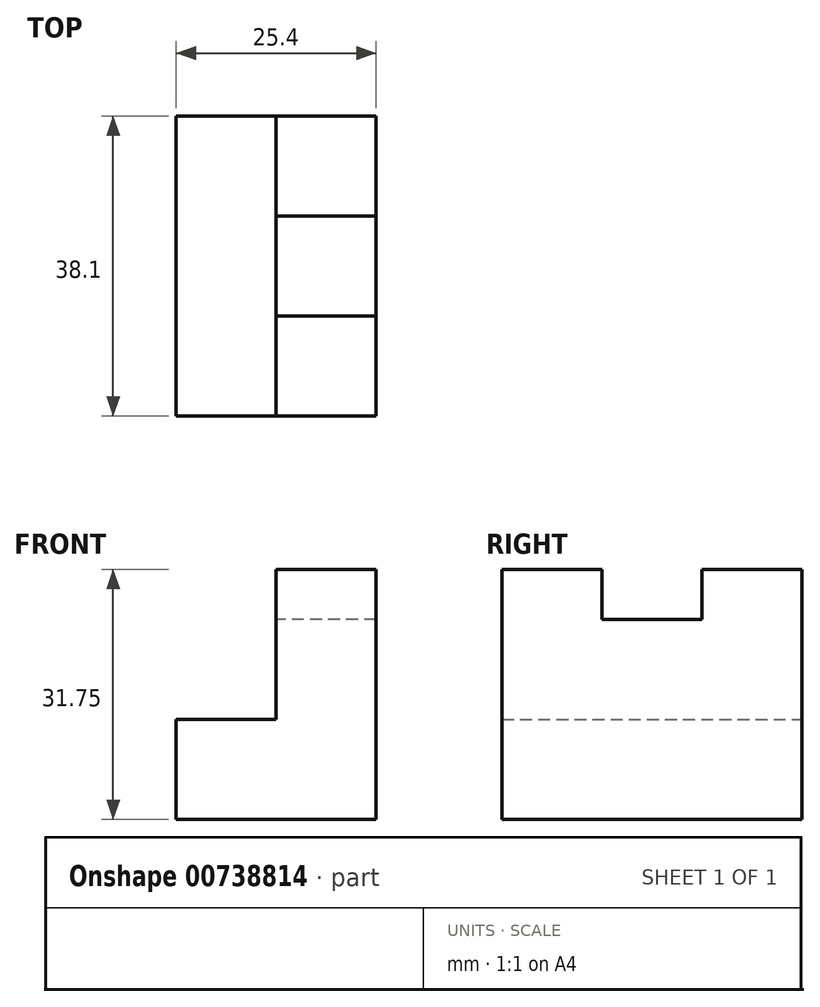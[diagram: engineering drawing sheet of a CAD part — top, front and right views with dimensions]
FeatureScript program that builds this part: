
annotation { "Feature Type Name" : "Feature", "Feature Type Description" : "" }
export const myFeature = defineFeature(function(context is Context, id is Id, definition is map)
    precondition{}
    {
        {
            var Q0;
            Q0=qCreatedBy(makeId("Front.planeOp"),FACE);
            var sketch = newSketch(context, id + "F0", { "sketchPlane" : qUnion([Q0])});
            skLineSegment(sketch, "E0", {"start": v(0, 0) * mm, "end": v(0, 31.75) * mm});
            skLineSegment(sketch, "E1", {"start": v(0, 31.75) * mm, "end": v(-12.7, 31.75) * mm});
            skLineSegment(sketch, "E2", {"start": v(-12.7, 31.75) * mm, "end": v(-12.7, 12.7) * mm});
            skLineSegment(sketch, "E3", {"start": v(-12.7, 12.7) * mm, "end": v(-25.4, 12.7) * mm});
            skLineSegment(sketch, "E4", {"start": v(-25.4, 12.7) * mm, "end": v(-25.4, 0) * mm});
            skLineSegment(sketch, "E5", {"start": v(-25.4, 0) * mm, "end": v(0, 0) * mm});
            skLineSegment(sketch, "E6", {"start": v(-25.4, 12.7) * mm, "end": v(-25.4, 12.7) * mm});
            skSolve(sketch);
        }
        {
            var Q0;
            Q0 = qSketchRegion(id + "F0", true);
            extrude(context, id + "F1", {"entities" : qUnion([Q0]), "depth" : 25.4 * mm, "offsetDistance" : 25.4 * mm});
        }
        {
            var Q0;
            Q0=makeQuery(id+"F1.opExtrude","SWEPT_FACE",FACE,{"disambiguationData":[OSD([sQuery(id+"F0.wireOp",EDGE,"E2")])]});
            var sketch = newSketch(context, id + "F2", { "sketchPlane" : qUnion([Q0])});
            skLineSegment(sketch, "E7", {"start": v(12.7, 31.75) * mm, "end": v(12.7, 25.4) * mm});
            skLineSegment(sketch, "E8", {"start": v(12.7, 25.4) * mm, "end": v(25.4, 25.4) * mm});
            skLineSegment(sketch, "E9", {"start": v(25.4, 25.4) * mm, "end": v(25.4, 31.75) * mm});
            skSolve(sketch);
        }
        {
            var Q0;
            Q0 = qSketchRegion(id + "F2", true);
            var Q1;
            Q1=makeQuery(id+"F1.opExtrude","CAP_FACE",FACE,{"disambiguationData":[OSD([sQuery(id+"F0.wireOp",EDGE,"E0"),sQuery(id+"F0.wireOp",EDGE,"E1"),sQuery(id+"F0.wireOp",EDGE,"E2"),sQuery(id+"F0.wireOp",EDGE,"E3"),sQuery(id+"F0.wireOp",EDGE,"E4"),sQuery(id+"F0.wireOp",EDGE,"E5")])],"isStart":false});
            extrude(context, id + "F3", {"entities" : qUnion([Q0, Q1]), "operationType" : NewBodyOperationType.ADD, "depth" : 12.7 * mm, "offsetDistance" : 25.4 * mm});
        }
        {
            var Q0;
            {var subQ0=sQuery(id+"F2.wireOp",EDGE,"E7");Q0=makeQuery(id+"F2.imprint","IMPRINT",FACE,{"disambiguationData":[TD([[makeQuery(id+"F2.imprint","IMPRINT",EDGE,{"derivedFrom":subQ0}),1.0]])]});}
            extrude(context, id + "F4", {"entities" : qUnion([Q0]), "operationType" : NewBodyOperationType.REMOVE, "endBound" : BoundingType.THROUGH_ALL, "oppositeDirection" : true, "depth" : 25.4 * mm, "offsetDistance" : 25.4 * mm});
        }
    });
